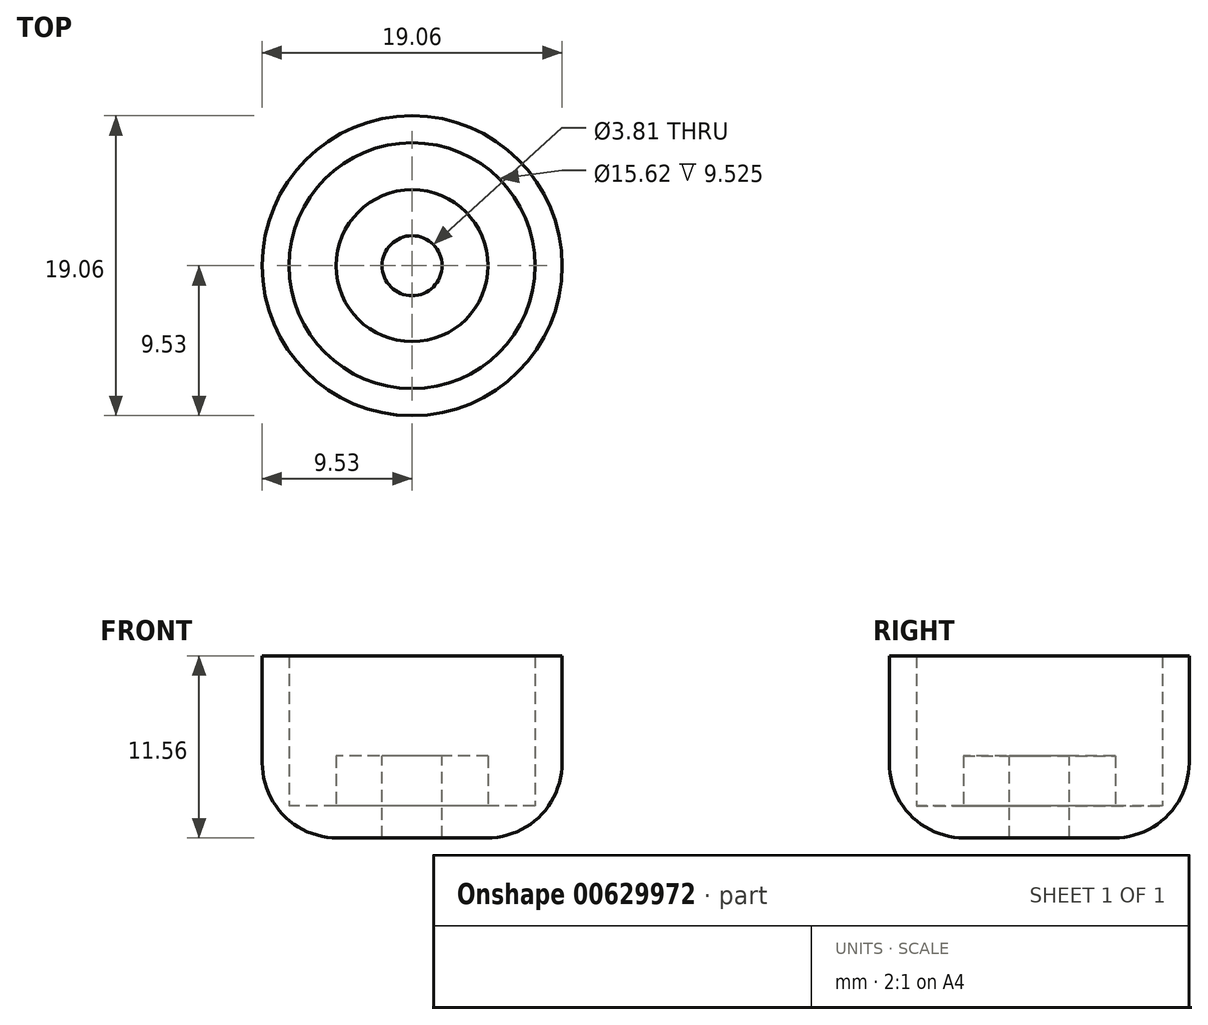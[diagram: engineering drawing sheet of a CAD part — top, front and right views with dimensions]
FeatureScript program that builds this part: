
annotation { "Feature Type Name" : "Feature", "Feature Type Description" : "" }
export const myFeature = defineFeature(function(context is Context, id is Id, definition is map)
    precondition{}
    {
        {
            var Q0;
            Q0=qCreatedBy(makeId("Top.planeOp"),FACE);
            var sketch = newSketch(context, id + "F0", { "sketchPlane" : qUnion([Q0])});
            skCircle(sketch, "E0", {"center": v(0, 0) * mm, "radius": 4.83 * mm});
            skCircle(sketch, "E1", {"center": v(0, 0) * mm, "radius": 6.1 * mm});
            skCircle(sketch, "E2", {"center": v(0, 0) * mm, "radius": 7.81 * mm});
            skCircle(sketch, "E3", {"center": v(0, 0) * mm, "radius": 9.53 * mm});
            skCircle(sketch, "E4", {"center": v(0, 0) * mm, "radius": 1.9 * mm});
            skSolve(sketch);
        }
        {
            var Q0;
            Q0=makeQuery(id+"F0.imprint","IMPRINT",FACE,{"disambiguationData":[TD([[makeQuery(id+"F0.imprint","IMPRINT",EDGE,{"derivedFrom":sQuery(id+"F0.wireOp",EDGE,"E2")}),-1.0]])]});
            var Q1;
            Q1=makeQuery(id+"F0.imprint","IMPRINT",FACE,{"disambiguationData":[TD([[makeQuery(id+"F0.imprint","IMPRINT",EDGE,{"derivedFrom":sQuery(id+"F0.wireOp",EDGE,"E1")}),-1.0]])]});
            var Q2;
            Q2=makeQuery(id+"F0.imprint","IMPRINT",FACE,{"disambiguationData":[TD([[makeQuery(id+"F0.imprint","IMPRINT",EDGE,{"derivedFrom":sQuery(id+"F0.wireOp",EDGE,"E0")}),-1.0]])]});
            var Q3;
            Q3=makeQuery(id+"F0.imprint","IMPRINT",FACE,{"disambiguationData":[TD([[makeQuery(id+"F0.imprint","IMPRINT",EDGE,{"derivedFrom":sQuery(id+"F0.wireOp",EDGE,"E0")}),1.0]])]});
            extrude(context, id + "F1", {"entities" : qUnion([Q0, Q1, Q2, Q3]), "oppositeDirection" : true, "depth" : 2.03 * mm, "offsetDistance" : 25.4 * mm});
        }
        {
            var Q0;
            Q0=makeQuery(id+"F0.imprint","IMPRINT",FACE,{"disambiguationData":[TD([[makeQuery(id+"F0.imprint","IMPRINT",EDGE,{"derivedFrom":sQuery(id+"F0.wireOp",EDGE,"E2")}),-1.0]])]});
            extrude(context, id + "F2", {"entities" : qUnion([Q0]), "operationType" : NewBodyOperationType.ADD, "depth" : 9.52 * mm, "offsetDistance" : 25.4 * mm});
        }
        {
            var Q0;
            Q0=makeQuery(id+"F1.opExtrude","CAP_EDGE",EDGE,{"disambiguationData":[OSD([sQuery(id+"F0.wireOp",EDGE,"E3")])],"isStart":false});
            fillet(context, id + "F3", {"entities" : qUnion([Q0]), "radius" : 4.76 * mm, "tangentPropagation" : true, "allowEdgeOverflow" : false});
        }
        {
            var Q0;
            Q0=makeQuery(id+"F0.imprint","IMPRINT",FACE,{"disambiguationData":[TD([[makeQuery(id+"F0.imprint","IMPRINT",EDGE,{"derivedFrom":sQuery(id+"F0.wireOp",EDGE,"E0")}),1.0]])]});
            extrude(context, id + "F4", {"entities" : qUnion([Q0]), "operationType" : NewBodyOperationType.ADD, "depth" : 3.17 * mm, "offsetDistance" : 25.4 * mm});
        }
    });
